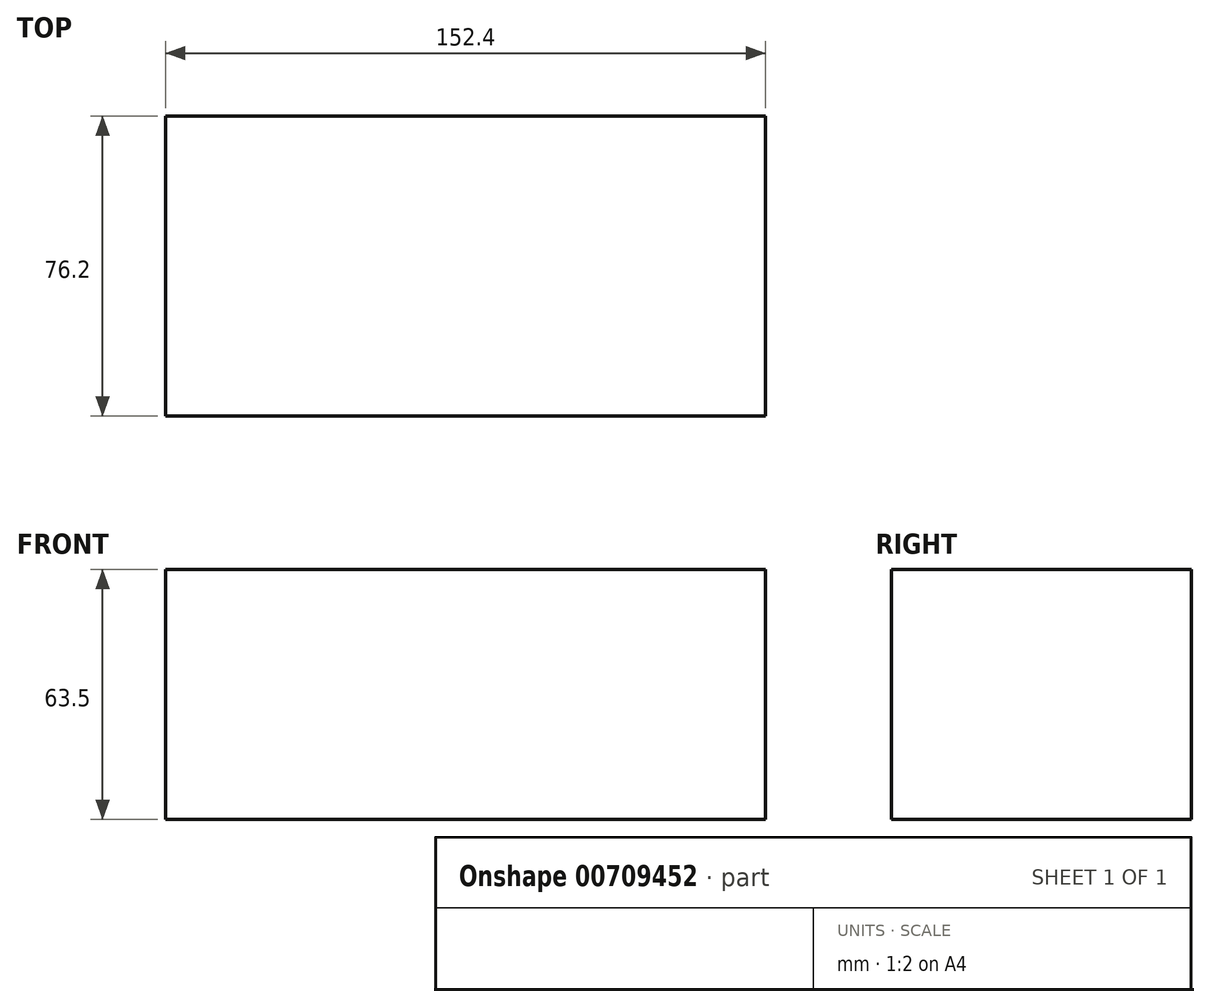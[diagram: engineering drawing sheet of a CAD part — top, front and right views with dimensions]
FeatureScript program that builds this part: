
annotation { "Feature Type Name" : "Feature", "Feature Type Description" : "" }
export const myFeature = defineFeature(function(context is Context, id is Id, definition is map)
    precondition{}
    {
        {
            var Q0;
            Q0=qCreatedBy(makeId("Front.planeOp"),FACE);
            var sketch = newSketch(context, id + "F0", { "sketchPlane" : qUnion([Q0])});
            skLineSegment(sketch, "E0.bottom", {"start": v(76.2, -31.75) * mm, "end": v(-76.2, -31.75) * mm});
            skLineSegment(sketch, "E0.top", {"start": v(76.2, 31.75) * mm, "end": v(-76.2, 31.75) * mm});
            skLineSegment(sketch, "E0.left", {"start": v(76.2, -31.75) * mm, "end": v(76.2, 31.75) * mm});
            skLineSegment(sketch, "E0.right", {"start": v(-76.2, -31.75) * mm, "end": v(-76.2, 31.75) * mm});
            skPoint(sketch, "E0.middle", {"position": v(0, 0) * mm});
            skSolve(sketch);
        }
        {
            var Q0;
            Q0=qSketchRegion(id+"F0",true);
            extrude(context, id + "F1", {"entities" : qUnion([Q0]), "depth" : 76.2 * mm, "offsetDistance" : 25.4 * mm});
        }
    });
